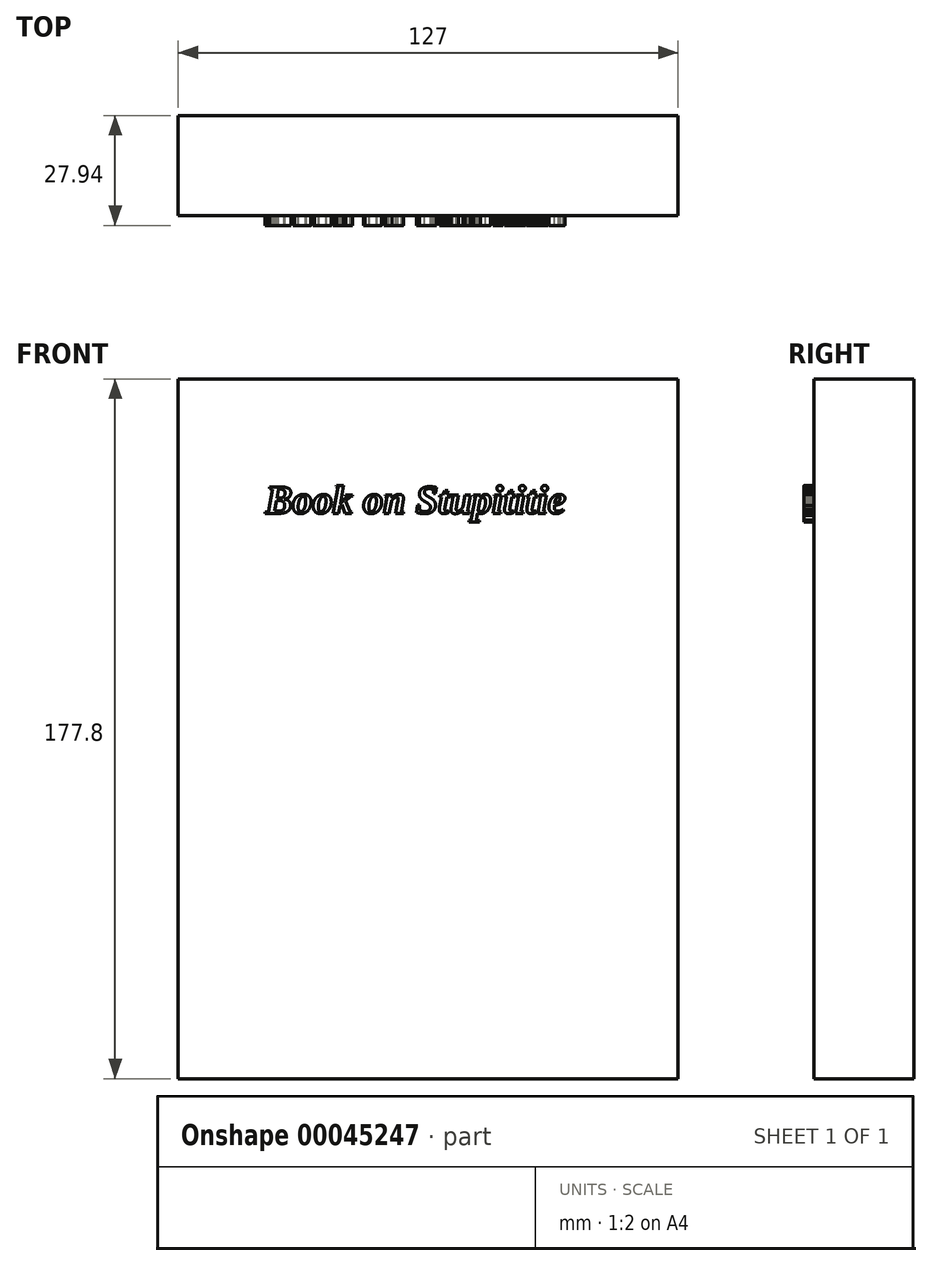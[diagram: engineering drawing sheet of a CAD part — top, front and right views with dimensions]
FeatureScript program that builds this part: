
annotation { "Feature Type Name" : "Feature", "Feature Type Description" : "" }
export const myFeature = defineFeature(function(context is Context, id is Id, definition is map)
    precondition{}
    {
        {
            var Q0;
            Q0=qCreatedBy(makeId("Front.planeOp"),FACE);
            var sketch = newSketch(context, id + "F0", { "sketchPlane" : qUnion([Q0])});
            skLineSegment(sketch, "E0.rect.bottom", {"start": v(63.5, -88.9) * mm, "end": v(-63.5, -88.9) * mm});
            skLineSegment(sketch, "E0.rect.top", {"start": v(63.5, 88.9) * mm, "end": v(-63.5, 88.9) * mm});
            skLineSegment(sketch, "E0.rect.left", {"start": v(63.5, -88.9) * mm, "end": v(63.5, 88.9) * mm});
            skLineSegment(sketch, "E0.rect.right", {"start": v(-63.5, -88.9) * mm, "end": v(-63.5, 88.9) * mm});
            skPoint(sketch, "E0.rect.middle", {"position": v(0, 0) * mm});
            skSolve(sketch);
        }
        {
            var Q0;
            Q0 = qSketchRegion(id + "F0", true);
            extrude(context, id + "F1", {"entities" : qUnion([Q0]), "depth" : 25.4 * mm});
        }
        {
            var Q0;
            Q0=makeQuery(id+"F1.opExtrude","SWEPT_FACE",FACE,{"disambiguationData":[OSD([sQuery(id+"F0.wireOp",EDGE,"E0.rect.top")])]});
            var sketch = newSketch(context, id + "F2", { "sketchPlane" : qUnion([Q0])});
            skLineSegment(sketch, "E1", {"start": v(-63.5, -6.35) * mm, "end": v(63.5, -6.35) * mm});
            skLineSegment(sketch, "E2", {"start": v(63.5, -12.7) * mm, "end": v(-63.5, -12.7) * mm});
            skPoint(sketch, "E2.endSnap0", {"position": v(-63.5, -12.7) * mm});
            skLineSegment(sketch, "E3", {"start": v(-63.5, -12.7) * mm, "end": v(-63.5, -19.05) * mm});
            skLineSegment(sketch, "E4", {"start": v(-63.5, -19.05) * mm, "end": v(63.5, -19.05) * mm});
            skLineSegment(sketch, "E5", {"start": v(63.5, -19.05) * mm, "end": v(63.5, -20.42) * mm});
            skSolve(sketch);
        }
        {
            var Q0;
            Q0=makeQuery(id+"F1.opExtrude","CAP_FACE",FACE,{"disambiguationData":[OSD([sQuery(id+"F0.wireOp",EDGE,"E0.rect.bottom"),sQuery(id+"F0.wireOp",EDGE,"E0.rect.top"),sQuery(id+"F0.wireOp",EDGE,"E0.rect.left"),sQuery(id+"F0.wireOp",EDGE,"E0.rect.right")])],"isStart":false});
            var sketch = newSketch(context, id + "F3", { "sketchPlane" : qUnion([Q0])});
            skText(sketch, "E6", { "text": "Book on Stupititie", "fontName": "Tinos-BoldItalic.ttf"});
            const initialGuessF3  = {"E6": [-0.04134, 0.05474, 1, 0, 0.00738]};
            skSetInitialGuess(sketch, initialGuessF3);
            skSolve(sketch);
        }
        {
            var Q0;
            Q0 = qSketchRegion(id + "F3", true);
            extrude(context, id + "F4", {"entities" : qUnion([Q0]), "operationType" : NewBodyOperationType.ADD, "depth" : 2.54 * mm});
        }
    });
